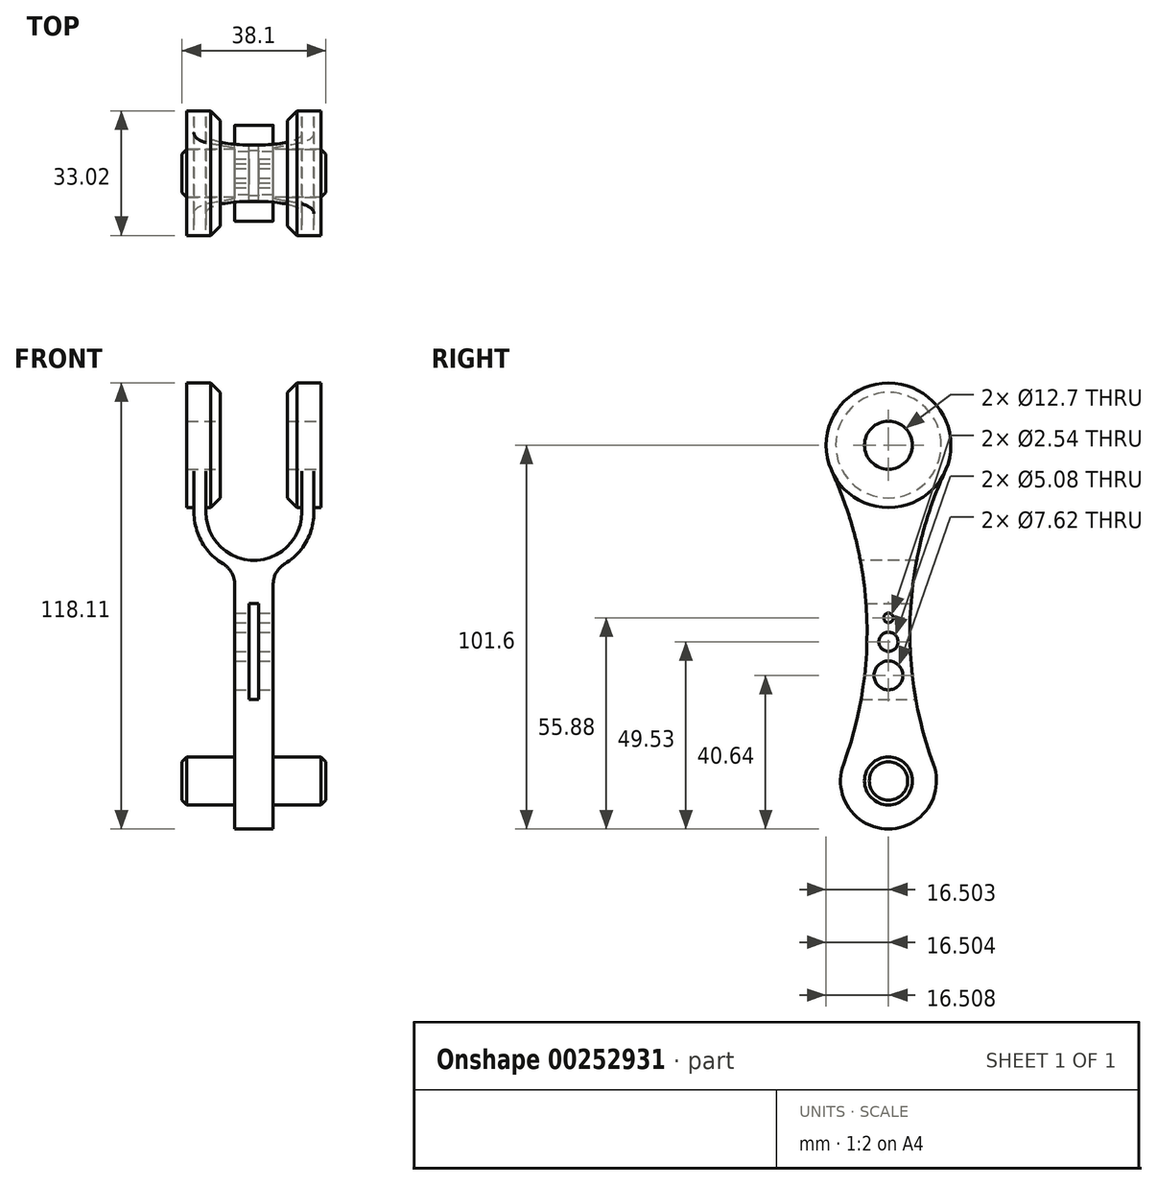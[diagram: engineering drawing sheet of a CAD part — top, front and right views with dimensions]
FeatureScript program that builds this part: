
annotation { "Feature Type Name" : "Feature", "Feature Type Description" : "" }
export const myFeature = defineFeature(function(context is Context, id is Id, definition is map)
    precondition{}
    {
        {
            var Q0;
            Q0=qCreatedBy(makeId("Front.planeOp"),FACE);
            var sketch = newSketch(context, id + "F0", { "sketchPlane" : qUnion([Q0])});
            skPoint(sketch, "E0.middle", {"position": v(0, 0) * mm});
            skArc(sketch, "E1", {"start": v(-8.17, -19.4) * mm, "mid": v(-13.82, -25.2) * mm, "end": v(-15.88, -33.02) * mm});
            skLineSegment(sketch, "E2.bottom", {"start": v(-5.08, 15.05) * mm, "end": v(5.08, 15.05) * mm});
            skLineSegment(sketch, "E2.left", {"start": v(-5.08, 15.05) * mm, "end": v(-5.08, -13.95) * mm});
            skLineSegment(sketch, "E2.right", {"start": v(5.08, 15.05) * mm, "end": v(5.08, -13.95) * mm});
            skArc(sketch, "E3", {"start": v(12.7, -33.02) * mm, "mid": v(0, -20.32) * mm, "end": v(-12.7, -33.02) * mm});
            skLineSegment(sketch, "E4.top", {"start": v(14.22, -50.8) * mm, "end": v(14.36, -50.8) * mm});
            skLineSegment(sketch, "E4.left", {"start": v(12.7, -33.02) * mm, "end": v(12.7, -49.28) * mm});
            skLineSegment(sketch, "E4.right", {"start": v(15.88, -33.02) * mm, "end": v(15.88, -49.28) * mm});
            skLineSegment(sketch, "E5.top", {"start": v(-14.36, -50.8) * mm, "end": v(-14.22, -50.8) * mm});
            skLineSegment(sketch, "E5.left", {"start": v(-15.88, -33.02) * mm, "end": v(-15.88, -49.28) * mm});
            skLineSegment(sketch, "E5.right", {"start": v(-12.7, -33.02) * mm, "end": v(-12.7, -49.28) * mm});
            skArc(sketch, "E6.trimOffspring", {"start": v(15.88, -33.02) * mm, "mid": v(13.82, -25.2) * mm, "end": v(8.17, -19.4) * mm});
            skPoint(sketch, "E7.visualSharp", {"position": v(-5.08, -17.97) * mm});
            skArc(sketch, "E7.filletArc", {"start": v(-8.17, -19.4) * mm, "mid": v(-5.9, -17.08) * mm, "end": v(-5.08, -13.95) * mm});
            skPoint(sketch, "E8.visualSharp", {"position": v(5.08, -17.97) * mm});
            skArc(sketch, "E8.filletArc", {"start": v(5.08, -13.95) * mm, "mid": v(5.9, -17.08) * mm, "end": v(8.17, -19.4) * mm});
            skArc(sketch, "E9.filletArc", {"start": v(12.7, -49.28) * mm, "mid": v(13.15, -50.35) * mm, "end": v(14.22, -50.8) * mm});
            skArc(sketch, "E10.filletArc", {"start": v(14.36, -50.8) * mm, "mid": v(15.44, -50.35) * mm, "end": v(15.88, -49.28) * mm});
            skArc(sketch, "E11.filletArc", {"start": v(-15.88, -49.28) * mm, "mid": v(-15.44, -50.35) * mm, "end": v(-14.36, -50.8) * mm});
            skArc(sketch, "E12.filletArc", {"start": v(-14.22, -50.8) * mm, "mid": v(-13.15, -50.35) * mm, "end": v(-12.7, -49.28) * mm});
            skSolve(sketch);
        }
        {
            var Q0;
            Q0=qSketchRegion(id+"F0",true);
            extrude(context, id + "F1", {"entities" : qUnion([Q0]), "endBound" : BoundingType.SYMMETRIC, "depth" : 38.1 * mm});
        }
        {
            var Q0;
            Q0=qCreatedBy(makeId("Right.planeOp"),FACE);
            var sketch = newSketch(context, id + "F2", { "sketchPlane" : qUnion([Q0])});
            skCircle(sketch, "E13", {"center": v(0, -50.8) * mm, "radius": 6.35 * mm});
            skSolve(sketch);
        }
        {
            var Q0;
            Q0=qCreatedBy(makeId("Right.planeOp"),FACE);
            var sketch = newSketch(context, id + "F3", { "sketchPlane" : qUnion([Q0])});
            skCircle(sketch, "E14", {"center": v(0, -50.8) * mm, "radius": 16.51 * mm});
            skSolve(sketch);
        }
        {
            var Q0;
            Q0=qSketchRegion(id+"F3",true);
            extrude(context, id + "F4", {"entities" : qUnion([Q0]), "operationType" : NewBodyOperationType.ADD, "endBound" : BoundingType.SYMMETRIC, "depth" : 35.56 * mm});
        }
        {
            var Q0;
            Q0=qCreatedBy(makeId("Front.planeOp"),FACE);
            var sketch = newSketch(context, id + "F5", { "sketchPlane" : qUnion([Q0])});
            skLineSegment(sketch, "E15.bottom", {"start": v(8.9, -69.85) * mm, "end": v(-8.89, -69.85) * mm});
            skLineSegment(sketch, "E15.top", {"start": v(8.9, -31.75) * mm, "end": v(-8.89, -31.75) * mm});
            skLineSegment(sketch, "E15.left", {"start": v(8.9, -69.85) * mm, "end": v(8.9, -31.75) * mm});
            skLineSegment(sketch, "E15.right", {"start": v(-8.89, -69.85) * mm, "end": v(-8.89, -31.75) * mm});
            skPoint(sketch, "E15.middle", {"position": v(0, -50.8) * mm});
            skSolve(sketch);
        }
        {
            var Q0;
            Q0=qSketchRegion(id+"F2",true);
            extrude(context, id + "F6", {"entities" : qUnion([Q0]), "operationType" : NewBodyOperationType.REMOVE, "endBound" : BoundingType.SYMMETRIC, "oppositeDirection" : true, "depth" : 76.2 * mm});
        }
        {
            var Q0;
            Q0=qSketchRegion(id+"F5",true);
            extrude(context, id + "F7", {"entities" : qUnion([Q0]), "operationType" : NewBodyOperationType.REMOVE, "endBound" : BoundingType.SYMMETRIC, "oppositeDirection" : true, "depth" : 38.1 * mm});
        }
        {
            var Q0;
            Q0=makeQuery(id+"F7.boolean.opBoolean","INTERSECT",EDGE,{"derivedFrom":[makeQuery(id+"F4.opExtrude","SWEPT_FACE",FACE,{"disambiguationData":[OSD([sQuery(id+"F3.wireOp",EDGE,"E14")])]}),makeQuery(id+"F7.opExtrude","SWEPT_FACE",FACE,{"disambiguationData":[OSD([sQuery(id+"F5.wireOp",EDGE,"E15.right")])]})]});
            var Q1;
            Q1=makeQuery(id+"F7.boolean.opBoolean","INTERSECT",EDGE,{"derivedFrom":[makeQuery(id+"F4.opExtrude","SWEPT_FACE",FACE,{"disambiguationData":[OSD([sQuery(id+"F3.wireOp",EDGE,"E14")])]}),makeQuery(id+"F7.opExtrude","SWEPT_FACE",FACE,{"disambiguationData":[OSD([sQuery(id+"F5.wireOp",EDGE,"E15.left")])]})]});
            chamfer(context, id + "F8", {"entities" : qUnion([Q0, Q1]), "width" : 2.54 * mm, "tangentPropagation" : true});
        }
        {
            var Q0;
            Q0=qCreatedBy(makeId("Right.planeOp"),FACE);
            var sketch = newSketch(context, id + "F9", { "sketchPlane" : qUnion([Q0])});
            skArc(sketch, "E16", {"start": v(19.05, 38.09) * mm, "mid": v(0, 57.15) * mm, "end": v(-19.05, 38.09) * mm});
            skLineSegment(sketch, "E17.top", {"start": v(-19.05, 12.69) * mm, "end": v(19.05, 12.69) * mm});
            skLineSegment(sketch, "E17.left", {"start": v(-19.05, 38.09) * mm, "end": v(-19.05, 12.69) * mm});
            skLineSegment(sketch, "E17.right", {"start": v(19.05, 38.09) * mm, "end": v(19.05, 12.69) * mm});
            skSolve(sketch);
        }
        {
            var Q0;
            Q0=qSketchRegion(id+"F9",true);
            extrude(context, id + "F10", {"entities" : qUnion([Q0]), "operationType" : NewBodyOperationType.ADD, "endBound" : BoundingType.SYMMETRIC, "depth" : 10.16 * mm});
        }
        {
            var Q0;
            Q0=qCreatedBy(makeId("Right.planeOp"),FACE);
            var sketch = newSketch(context, id + "F11", { "sketchPlane" : qUnion([Q0])});
            skCircle(sketch, "E18", {"center": v(0, 38.1) * mm, "radius": 6.35 * mm});
            skSolve(sketch);
        }
        {
            var Q0;
            Q0=qSketchRegion(id+"F11",true);
            extrude(context, id + "F12", {"entities" : qUnion([Q0]), "operationType" : NewBodyOperationType.ADD, "endBound" : BoundingType.SYMMETRIC, "depth" : 38.1 * mm});
        }
        {
            var Q0;
            Q0=makeQuery(id+"F12.opExtrude","CAP_EDGE",EDGE,{"disambiguationData":[OSD([sQuery(id+"F11.wireOp",EDGE,"E18")])],"isStart":true});
            var Q1;
            Q1=makeQuery(id+"F12.opExtrude","CAP_EDGE",EDGE,{"disambiguationData":[OSD([sQuery(id+"F11.wireOp",EDGE,"E18")])],"isStart":false});
            chamfer(context, id + "F13", {"entities" : qUnion([Q0, Q1]), "width" : 1.27 * mm, "tangentPropagation" : true});
        }
        {
            var Q0;
            Q0=qCreatedBy(makeId("Right.planeOp"),FACE);
            var sketch = newSketch(context, id + "F14", { "sketchPlane" : qUnion([Q0])});
            skArc(sketch, "E19", {"start": v(11.92, 33.71) * mm, "mid": v(0, 50.8) * mm, "end": v(-11.92, 33.71) * mm});
            skArc(sketch, "E20", {"start": v(-15, -43.9) * mm, "mid": v(0, -67.31) * mm, "end": v(15, -43.9) * mm});
            skArc(sketch, "E21", {"start": v(11.92, 33.71) * mm, "mid": v(5.75, -5.4) * mm, "end": v(15, -43.9) * mm});
            skPoint(sketch, "E22.center.orphan", {"position": v(45.72, -6.35) * mm});
            skPoint(sketch, "E23.center.orphan", {"position": v(-45.72, -6.35) * mm});
            skArc(sketch, "E24", {"start": v(-15, -43.9) * mm, "mid": v(-5.75, -5.4) * mm, "end": v(-11.92, 33.71) * mm});
            skSolve(sketch);
        }
        {
            var Q0;
            Q0=qSketchRegion(id+"F14",true);
            extrude(context, id + "F15", {"entities" : qUnion([Q0]), "operationType" : NewBodyOperationType.INTERSECT, "endBound" : BoundingType.SYMMETRIC, "depth" : 76.2 * mm});
        }
        {
            var Q0;
            Q0=qCreatedBy(makeId("Front.planeOp"),FACE);
            var sketch = newSketch(context, id + "F16", { "sketchPlane" : qUnion([Q0])});
            skLineSegment(sketch, "E25.bottom", {"start": v(-1.27, -8.87) * mm, "end": v(1.27, -8.87) * mm});
            skLineSegment(sketch, "E25.top", {"start": v(-1.27, 16.53) * mm, "end": v(1.27, 16.53) * mm});
            skLineSegment(sketch, "E25.left", {"start": v(-1.27, -8.87) * mm, "end": v(-1.27, 16.53) * mm});
            skLineSegment(sketch, "E25.right", {"start": v(1.27, -8.87) * mm, "end": v(1.27, 16.53) * mm});
            skSolve(sketch);
        }
        {
            var Q0;
            Q0=qSketchRegion(id+"F16",true);
            extrude(context, id + "F17", {"entities" : qUnion([Q0]), "operationType" : NewBodyOperationType.REMOVE, "endBound" : BoundingType.SYMMETRIC, "oppositeDirection" : true, "depth" : 50.8 * mm});
        }
        {
            var Q0;
            Q0=qCreatedBy(makeId("Right.planeOp"),FACE);
            var sketch = newSketch(context, id + "F18", { "sketchPlane" : qUnion([Q0])});
            skCircle(sketch, "E26", {"center": v(0, 10.16) * mm, "radius": 3.81 * mm});
            skCircle(sketch, "E27", {"center": v(0, 1.27) * mm, "radius": 2.54 * mm});
            skCircle(sketch, "E28", {"center": v(0, -5.08) * mm, "radius": 1.27 * mm});
            skSolve(sketch);
        }
        {
            var Q0;
            Q0=qSketchRegion(id+"F18",true);
            extrude(context, id + "F19", {"entities" : qUnion([Q0]), "operationType" : NewBodyOperationType.REMOVE, "endBound" : BoundingType.SYMMETRIC, "oppositeDirection" : true, "depth" : 25.4 * mm});
        }
        {
            var Q0;
            Q0=makeQuery(id+"F1.opExtrude","SWEPT_BODY",BODY,{"disambiguationData":[OSD([sQuery(id+"F0.wireOp",EDGE,"E1"),sQuery(id+"F0.wireOp",EDGE,"E2.bottom"),sQuery(id+"F0.wireOp",EDGE,"E2.left"),sQuery(id+"F0.wireOp",EDGE,"E2.right"),sQuery(id+"F0.wireOp",EDGE,"E3"),sQuery(id+"F0.wireOp",EDGE,"E4.top"),sQuery(id+"F0.wireOp",EDGE,"E4.left"),sQuery(id+"F0.wireOp",EDGE,"E4.right"),sQuery(id+"F0.wireOp",EDGE,"E5.top"),sQuery(id+"F0.wireOp",EDGE,"E5.left"),sQuery(id+"F0.wireOp",EDGE,"E5.right"),sQuery(id+"F0.wireOp",EDGE,"E6.trimOffspring"),sQuery(id+"F0.wireOp",EDGE,"E7.filletArc"),sQuery(id+"F0.wireOp",EDGE,"E8.filletArc"),sQuery(id+"F0.wireOp",EDGE,"E9.filletArc"),sQuery(id+"F0.wireOp",EDGE,"E10.filletArc"),sQuery(id+"F0.wireOp",EDGE,"E11.filletArc"),sQuery(id+"F0.wireOp",EDGE,"E12.filletArc")])]});
            var Q1;
            {var subQ0=sQuery(id+"F11.wireOp",EDGE,"E18");Q1=makeQuery(id+"F13.opChamfer","BLEND_EDGE",EDGE,{"blendedFrom":[makeQuery(id+"F12.opExtrude","CAP_EDGE",EDGE,{"disambiguationData":[OSD([subQ0])],"isStart":false}),makeQuery(id+"F12.opExtrude","CAP_FACE",FACE,{"disambiguationData":[OSD([subQ0])],"isStart":false})],"blendedInto":[makeQuery(id+"F12.opExtrude","CAP_FACE",FACE,{"disambiguationData":[OSD([subQ0])],"isStart":false})]});}
            transform(context, id + "F20", {"entities" : qUnion([Q0]), "transformType" : TransformType.ROTATION, "transformAxis" : qUnion([Q1]), "angle" : 3.14 * radian, "makeCopy" : false});
        }
        {
            var Q0;
            Q0=qCreatedBy(makeId("Front.planeOp"),FACE);
            var sketch = newSketch(context, id + "F21", { "sketchPlane" : qUnion([Q0])});
            skPoint(sketch, "E29", {"position": v(-17.78, 127) * mm});
            skLineSegment(sketch, "E30", {"start": v(-17.78, 127) * mm, "end": v(17.78, 127) * mm});
            skPoint(sketch, "E31", {"position": v(0, 127) * mm});
            skLineSegment(sketch, "E32", {"start": v(0, 127) * mm, "end": v(0, 0) * mm, "construction": true});
            skSolve(sketch);
        }
        {
            var Q0;
            Q0=makeQuery(id+"F1.opExtrude","SWEPT_BODY",BODY,{"disambiguationData":[OSD([sQuery(id+"F0.wireOp",EDGE,"E1"),sQuery(id+"F0.wireOp",EDGE,"E2.bottom"),sQuery(id+"F0.wireOp",EDGE,"E2.left"),sQuery(id+"F0.wireOp",EDGE,"E2.right"),sQuery(id+"F0.wireOp",EDGE,"E3"),sQuery(id+"F0.wireOp",EDGE,"E4.top"),sQuery(id+"F0.wireOp",EDGE,"E4.left"),sQuery(id+"F0.wireOp",EDGE,"E4.right"),sQuery(id+"F0.wireOp",EDGE,"E5.top"),sQuery(id+"F0.wireOp",EDGE,"E5.left"),sQuery(id+"F0.wireOp",EDGE,"E5.right"),sQuery(id+"F0.wireOp",EDGE,"E6.trimOffspring"),sQuery(id+"F0.wireOp",EDGE,"E7.filletArc"),sQuery(id+"F0.wireOp",EDGE,"E8.filletArc"),sQuery(id+"F0.wireOp",EDGE,"E9.filletArc"),sQuery(id+"F0.wireOp",EDGE,"E10.filletArc"),sQuery(id+"F0.wireOp",EDGE,"E11.filletArc"),sQuery(id+"F0.wireOp",EDGE,"E12.filletArc")])]});
            var Q1;
            Q1=sQuery(id+"F21.wireOp",EDGE,"E32");
            transform(context, id + "F22", {"entities" : qUnion([Q0]), "transformType" : TransformType.TRANSLATION_ENTITY, "oppositeDirectionEntity" : false, "transformLine" : qUnion([Q1]), "makeCopy" : false});
        }
    });
